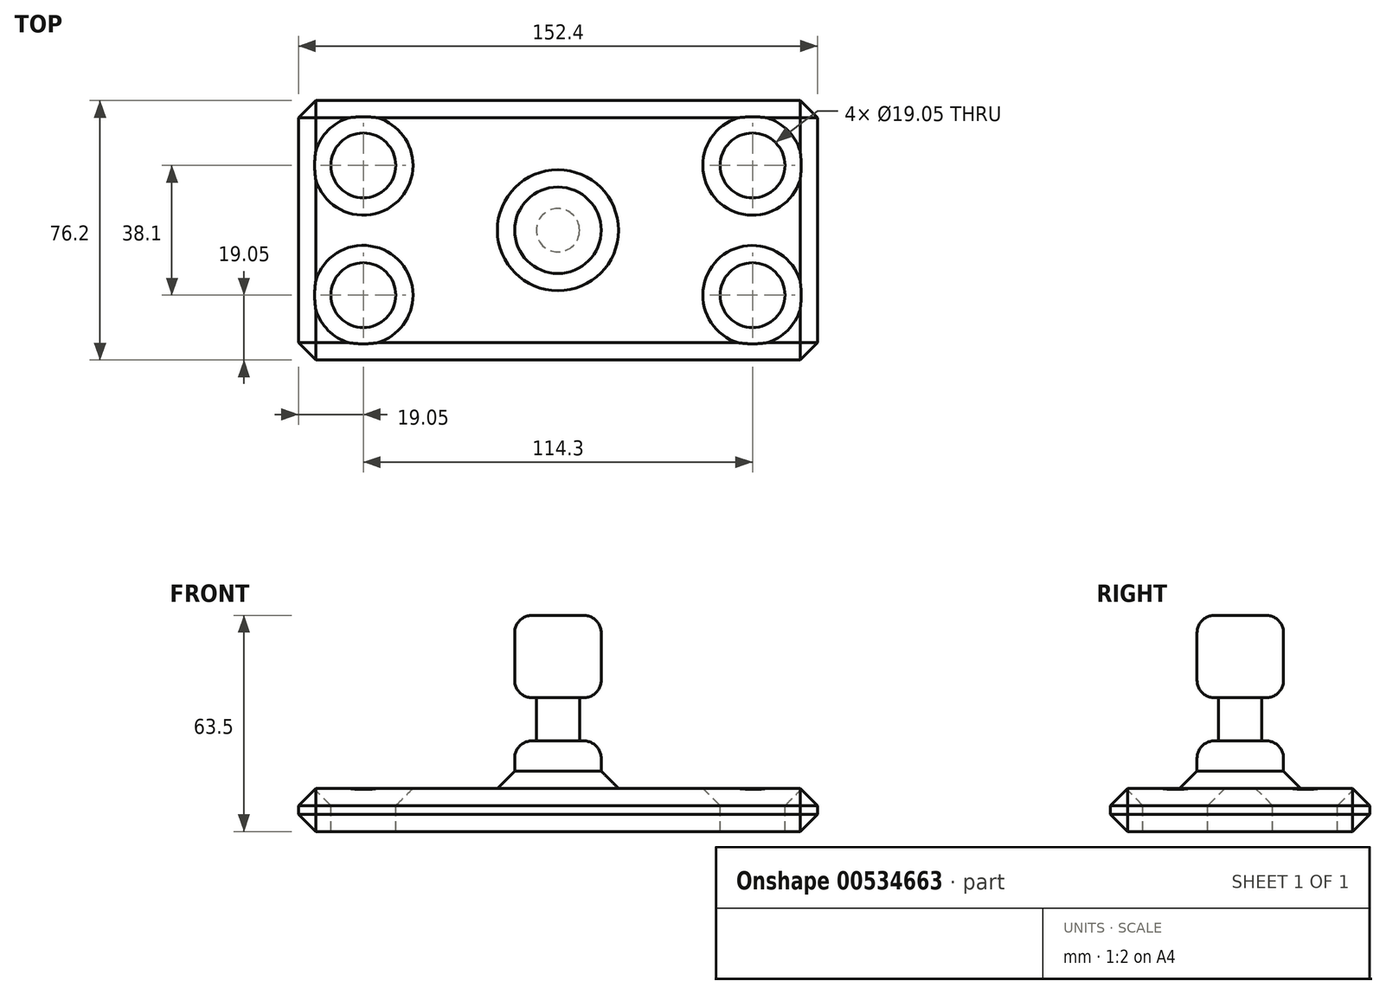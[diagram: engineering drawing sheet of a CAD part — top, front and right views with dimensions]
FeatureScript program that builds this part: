
annotation { "Feature Type Name" : "Feature", "Feature Type Description" : "" }
export const myFeature = defineFeature(function(context is Context, id is Id, definition is map)
    precondition{}
    {
        {
            var Q0;
            Q0=qCreatedBy(makeId("Top.planeOp"),FACE);
            var sketch = newSketch(context, id + "F0", { "sketchPlane" : qUnion([Q0])});
            skLineSegment(sketch, "E0.bottom", {"start": v(76.2, 38.1) * mm, "end": v(-76.2, 38.1) * mm});
            skLineSegment(sketch, "E0.top", {"start": v(76.2, -38.1) * mm, "end": v(-76.2, -38.1) * mm});
            skLineSegment(sketch, "E0.left", {"start": v(76.2, 38.1) * mm, "end": v(76.2, -38.1) * mm});
            skLineSegment(sketch, "E0.right", {"start": v(-76.2, 38.1) * mm, "end": v(-76.2, -38.1) * mm});
            skPoint(sketch, "E0.middle", {"position": v(0, 0) * mm});
            skSolve(sketch);
        }
        {
            var Q0;
            Q0=makeQuery(id+"F0.imprint","IMPRINT",FACE,{"disambiguationData":[TD([[makeQuery(id+"F0.imprint","IMPRINT",EDGE,{"derivedFrom":sQuery(id+"F0.wireOp",EDGE,"E0.bottom")}),1.0]])]});
            extrude(context, id + "F1", {"entities" : qUnion([Q0]), "depth" : 12.7 * mm, "offsetDistance" : 25.4 * mm});
        }
        {
            var Q0;
            Q0=qCreatedBy(makeId("Top.planeOp"),FACE);
            var sketch = newSketch(context, id + "F2", { "sketchPlane" : qUnion([Q0])});
            skCircle(sketch, "E1", {"center": v(-57.15, 19.05) * mm, "radius": 9.53 * mm});
            skCircle(sketch, "E2", {"center": v(57.15, 19.05) * mm, "radius": 9.53 * mm});
            skCircle(sketch, "E3", {"center": v(57.15, -19.05) * mm, "radius": 9.53 * mm});
            skCircle(sketch, "E4", {"center": v(-57.15, -19.05) * mm, "radius": 9.53 * mm});
            skSolve(sketch);
        }
        {
            var Q0;
            Q0 = qSketchRegion(id + "F2", true);
            var Q1;
            Q1=sQuery(id+"F2.wireOp",EDGE,"E1");
            extrude(context, id + "F3", {"entities" : qUnion([Q0]), "operationType" : NewBodyOperationType.REMOVE, "surfaceEntities" : qUnion([Q1]), "endBound" : BoundingType.SYMMETRIC, "oppositeDirection" : true, "depth" : 25.4 * mm, "offsetDistance" : 25.4 * mm});
        }
        {
            var Q0;
            Q0=qCreatedBy(makeId("Front.planeOp"),FACE);
            var sketch = newSketch(context, id + "F4", { "sketchPlane" : qUnion([Q0])});
            skLineSegment(sketch, "E5.bottom", {"start": v(0, 12.7) * mm, "end": v(12.7, 12.7) * mm});
            skLineSegment(sketch, "E5.top", {"start": v(0, 63.5) * mm, "end": v(12.7, 63.5) * mm});
            skLineSegment(sketch, "E5.left", {"start": v(0, 12.7) * mm, "end": v(0, 63.5) * mm});
            skLineSegment(sketch, "E5.right", {"start": v(12.7, 12.7) * mm, "end": v(12.7, 63.5) * mm});
            skSolve(sketch);
        }
        {
            var Q0;
            Q0=makeQuery(id+"F4.imprint","IMPRINT",FACE,{"disambiguationData":[TD([[makeQuery(id+"F4.imprint","IMPRINT",EDGE,{"derivedFrom":sQuery(id+"F4.wireOp",EDGE,"E5.bottom")}),1.0]])]});
            var Q1;
            Q1=sQuery(id+"F4.wireOp",EDGE,"E5.left");
            revolve(context, id + "F5", {"operationType" : NewBodyOperationType.ADD, "entities" : qUnion([Q0]), "axis" : qUnion([Q1]), "revolveType" : RevolveType.FULL});
        }
        {
            var Q0;
            Q0=qCreatedBy(makeId("Front.planeOp"),FACE);
            var sketch = newSketch(context, id + "F6", { "sketchPlane" : qUnion([Q0])});
            skLineSegment(sketch, "E6.bottom", {"start": v(6.35, 39.33) * mm, "end": v(13.97, 39.33) * mm});
            skLineSegment(sketch, "E6.top", {"start": v(6.35, 26.63) * mm, "end": v(13.97, 26.63) * mm});
            skLineSegment(sketch, "E6.left", {"start": v(6.35, 39.33) * mm, "end": v(6.35, 26.63) * mm});
            skLineSegment(sketch, "E6.right", {"start": v(13.97, 39.33) * mm, "end": v(13.97, 26.63) * mm});
            skSolve(sketch);
        }
        {
            var Q0;
            Q0=makeQuery(id+"F6.imprint","IMPRINT",FACE,{"disambiguationData":[TD([[makeQuery(id+"F6.imprint","IMPRINT",EDGE,{"derivedFrom":sQuery(id+"F6.wireOp",EDGE,"E6.bottom")}),-1.0]])]});
            var Q1;
            Q1=makeQuery(id+"F5.opRevolve","SWEPT_FACE",FACE,{"disambiguationData":[OSD([sQuery(id+"F4.wireOp",EDGE,"E5.right")])]});
            revolve(context, id + "F7", {"operationType" : NewBodyOperationType.REMOVE, "entities" : qUnion([Q0]), "axis" : qUnion([Q1]), "revolveType" : RevolveType.FULL, "oppositeDirection" : true});
        }
        {
            var Q0;
            Q0=makeQuery(id+"F5.opRevolve","SWEPT_EDGE",EDGE,{"disambiguationData":[OSD([sQuery(id+"F4.wireOp",EDGE,"E5.bottom"),sQuery(id+"F4.wireOp",EDGE,"E5.right")])]});
            var Q1;
            Q1=makeQuery(id+"F5.opRevolve","SWEPT_EDGE",EDGE,{"disambiguationData":[OSD([sQuery(id+"F4.wireOp",EDGE,"E5.top"),sQuery(id+"F4.wireOp",EDGE,"E5.right")])]});
            var Q2;
            Q2=makeQuery(id+"F7.boolean.opBoolean","INTERSECT",EDGE,{"derivedFrom":[makeQuery(id+"F5.opRevolve","SWEPT_FACE",FACE,{"disambiguationData":[OSD([sQuery(id+"F4.wireOp",EDGE,"E5.right")])]}),makeQuery(id+"F7.opRevolve","SWEPT_FACE",FACE,{"disambiguationData":[OSD([sQuery(id+"F6.wireOp",EDGE,"E6.top")])]})]});
            var Q3;
            Q3=makeQuery(id+"F7.boolean.opBoolean","INTERSECT",EDGE,{"derivedFrom":[makeQuery(id+"F5.opRevolve","SWEPT_FACE",FACE,{"disambiguationData":[OSD([sQuery(id+"F4.wireOp",EDGE,"E5.right")])]}),makeQuery(id+"F7.opRevolve","SWEPT_FACE",FACE,{"disambiguationData":[OSD([sQuery(id+"F6.wireOp",EDGE,"E6.bottom")])]})]});
            fillet(context, id + "F8", {"entities" : qUnion([Q0, Q1, Q2, Q3]), "radius" : 5.08 * mm, "tangentPropagation" : true, "allowEdgeOverflow" : false});
        }
        {
            var Q0;
            Q0=makeQuery(id+"F1.opExtrude","CAP_FACE",FACE,{"disambiguationData":[OSD([sQuery(id+"F0.wireOp",EDGE,"E0.bottom"),sQuery(id+"F0.wireOp",EDGE,"E0.top"),sQuery(id+"F0.wireOp",EDGE,"E0.left"),sQuery(id+"F0.wireOp",EDGE,"E0.right")])],"isStart":false});
            var Q1;
            Q1=makeQuery(id+"F1.opExtrude","CAP_EDGE",EDGE,{"disambiguationData":[OSD([sQuery(id+"F0.wireOp",EDGE,"E0.top")])],"isStart":true});
            var Q2;
            Q2=makeQuery(id+"F1.opExtrude","CAP_EDGE",EDGE,{"disambiguationData":[OSD([sQuery(id+"F0.wireOp",EDGE,"E0.bottom")])],"isStart":true});
            var Q3;
            Q3=makeQuery(id+"F1.opExtrude","SWEPT_FACE",FACE,{"disambiguationData":[OSD([sQuery(id+"F0.wireOp",EDGE,"E0.right")])]});
            var Q4;
            Q4=makeQuery(id+"F1.opExtrude","SWEPT_FACE",FACE,{"disambiguationData":[OSD([sQuery(id+"F0.wireOp",EDGE,"E0.left")])]});
            chamfer(context, id + "F9", {"entities" : qUnion([Q0, Q1, Q2, Q3, Q4]), "width" : 5.08 * mm, "tangentPropagation" : true});
        }
    });
